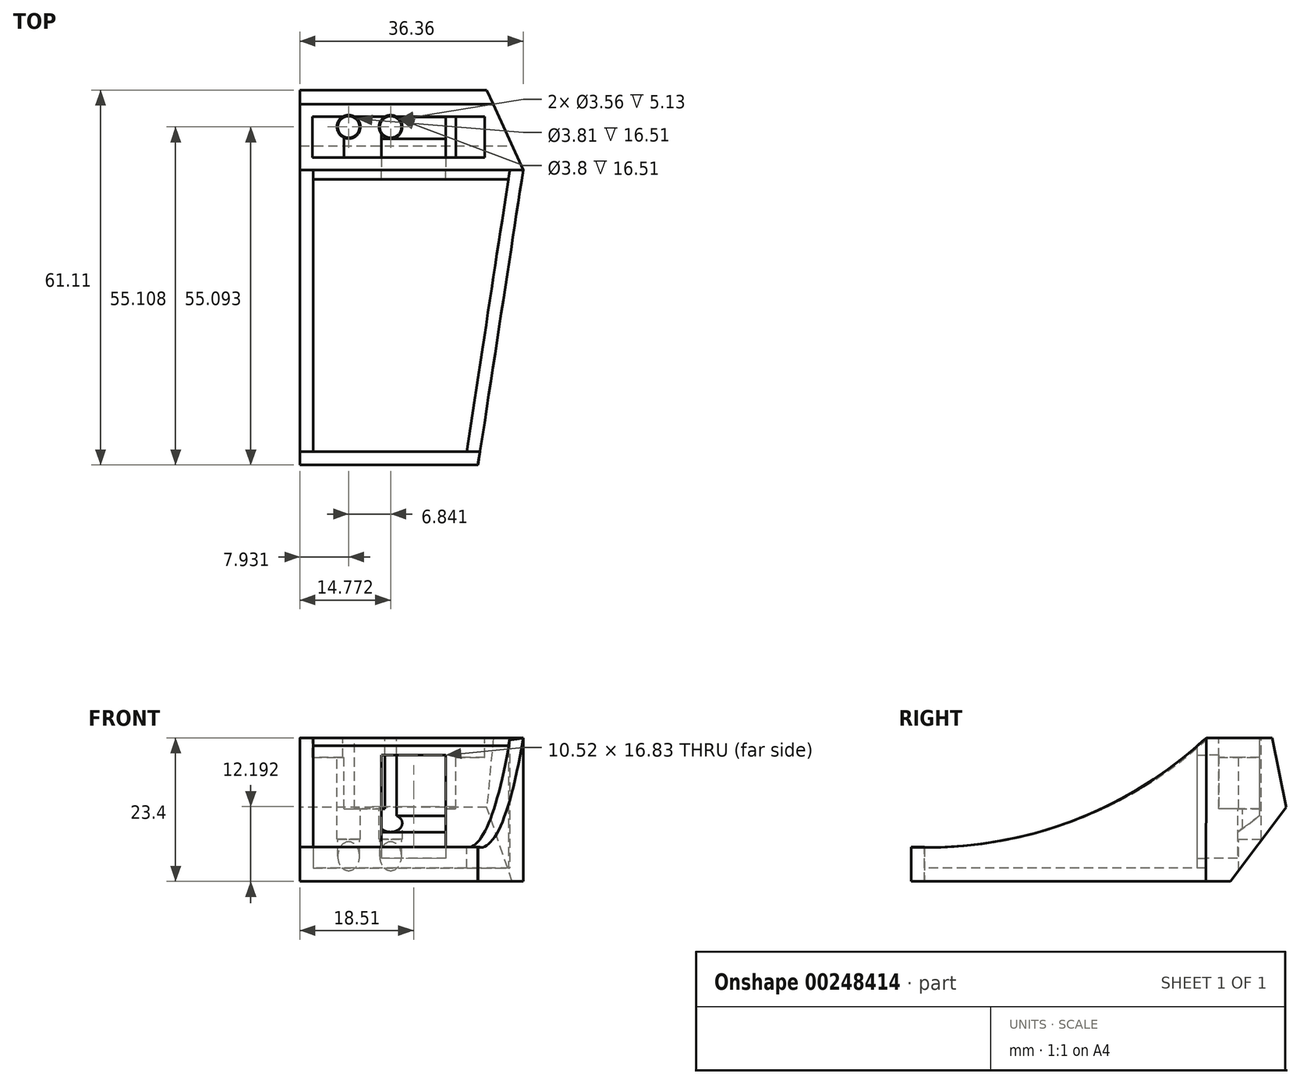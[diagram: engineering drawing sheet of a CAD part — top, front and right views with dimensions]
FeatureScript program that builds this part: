
annotation { "Feature Type Name" : "Feature", "Feature Type Description" : "" }
export const myFeature = defineFeature(function(context is Context, id is Id, definition is map)
    precondition{}
    {
        {
            var Q0;
            Q0=qCreatedBy(makeId("Top.planeOp"),FACE);
            var sketch = newSketch(context, id + "F0", { "sketchPlane" : qUnion([Q0])});
            skLineSegment(sketch, "E0", {"start": v(-18.5, 25.98) * mm, "end": v(-18.5, -25.98) * mm});
            skLineSegment(sketch, "E1", {"start": v(-18.5, -25.98) * mm, "end": v(10.5, -25.98) * mm});
            skLineSegment(sketch, "E2", {"start": v(10.5, -25.98) * mm, "end": v(18.45, 25.98) * mm});
            skLineSegment(sketch, "E3", {"start": v(-18.5, 25.98) * mm, "end": v(18.45, 25.98) * mm});
            skLineSegment(sketch, "E4", {"start": v(0, 0) * mm, "end": v(-18.5, 0) * mm});
            skSolve(sketch);
        }
        {
            var Q0;
            Q0 = qSketchRegion(id + "F0", true);
            extrude(context, id + "F1", {"entities" : qUnion([Q0]), "depth" : 2.16 * mm, "offsetDistance" : 25.4 * mm});
        }
        {
            var Q0;
            Q0=makeQuery(id+"F1.opExtrude","SWEPT_FACE",FACE,{"disambiguationData":[OSD([sQuery(id+"F0.wireOp",EDGE,"E0")])]});
            var sketch = newSketch(context, id + "F2", { "sketchPlane" : qUnion([Q0])});
            skLineSegment(sketch, "E5.MirrorCS", {"start": v(26, 0) * mm, "end": v(26, 5.58) * mm});
            skLineSegment(sketch, "E6.MirrorCS", {"start": v(-22.05, 23.4) * mm, "end": v(-22.05, 0) * mm});
            skLineSegment(sketch, "E7.MirrorCS", {"start": v(-22.05, 23.4) * mm, "end": v(-32.8, 23.38) * mm});
            skLineSegment(sketch, "E8.MirrorCS", {"start": v(-32.8, 23.38) * mm, "end": v(-35.1, 12.1) * mm});
            skLineSegment(sketch, "E9.MirrorCS", {"start": v(-25.98, 0) * mm, "end": v(-35.1, 12.1) * mm});
            skArc(sketch, "E10.MirrorCS", {"start": v(26, 5.58) * mm, "mid": v(0.2, 9.7) * mm, "end": v(-22.05, 23.4) * mm});
            skLineSegment(sketch, "E11.MirrorCS", {"start": v(26, 0) * mm, "end": v(-25.98, 0) * mm});
            skSolve(sketch);
        }
        {
            var Q0;
            {var subQ0=sQuery(id+"F2.wireOp",EDGE,"E11.MirrorCS");var subQ1=sQuery(id+"F2.wireOp",EDGE,"E6.MirrorCS");var subQ2=makeQuery(id+"F2.imprint","INTERSECT",VERTEX,{"derivedFrom":[subQ1,subQ0]});Q0=makeQuery(id+"F2.imprint","IMPRINT",FACE,{"disambiguationData":[TD([[makeQuery(id+"F2.imprint","IMPRINT",EDGE,{"disambiguationData":[TD([[subQ2,1.0]])],"derivedFrom":subQ1}),-1.0]])]});}
            var Q1;
            {var subQ1=sQuery(id+"F0.wireOp",EDGE,"E0");var subQ6=makeQuery(id+"F1.opExtrude","SWEPT_EDGE",EDGE,{"disambiguationData":[OSD([subQ1,sQuery(id+"F0.wireOp",EDGE,"E1")])]});Q1=makeQuery(id+"F2.imprint","IMPRINT",FACE,{"disambiguationData":[TD([[makeQuery(id+"F2.imprint","IMPRINT",EDGE,{"derivedFrom":subQ6}),-1.0]])]});}
            var Q2;
            {var subQ9=sQuery(id+"F2.wireOp",EDGE,"E5.MirrorCS");Q2=makeQuery(id+"F2.imprint","IMPRINT",FACE,{"disambiguationData":[TD([[makeQuery(id+"F2.imprint","IMPRINT",EDGE,{"derivedFrom":subQ9}),1.0]])]});}
            var Q3;
            {var subQ1=sQuery(id+"F0.wireOp",EDGE,"E0");var subQ6=makeQuery(id+"F1.opExtrude","SWEPT_EDGE",EDGE,{"disambiguationData":[OSD([subQ1,sQuery(id+"F0.wireOp",EDGE,"E3")])]});Q3=makeQuery(id+"F2.imprint","IMPRINT",FACE,{"disambiguationData":[TD([[makeQuery(id+"F2.imprint","IMPRINT",EDGE,{"derivedFrom":subQ6}),1.0]])]});}
            extrude(context, id + "F3", {"entities" : qUnion([Q0, Q1, Q2, Q3]), "operationType" : NewBodyOperationType.ADD, "oppositeDirection" : true, "depth" : 2.16 * mm, "offsetDistance" : 25.4 * mm});
        }
        {
            var Q0;
            Q0=makeQuery(id+"F1.opExtrude","SWEPT_FACE",FACE,{"disambiguationData":[OSD([sQuery(id+"F0.wireOp",EDGE,"E2")])]});
            var sketch = newSketch(context, id + "F4", { "sketchPlane" : qUnion([Q0])});
            skLineSegment(sketch, "E12", {"start": v(-24.1, 0) * mm, "end": v(-24.1, 5.58) * mm});
            skLineSegment(sketch, "E13", {"start": v(-24.1, 0) * mm, "end": v(24.54, 0) * mm});
            skLineSegment(sketch, "E14", {"start": v(24.5, 23.39) * mm, "end": v(24.54, 0) * mm});
            skArc(sketch, "E15", {"start": v(-24.1, 5.58) * mm, "mid": v(1.96, 9.68) * mm, "end": v(24.5, 23.39) * mm});
            skSolve(sketch);
        }
        {
            var Q0;
            {var subQ3=sQuery(id+"F4.wireOp",EDGE,"E15");Q0=makeQuery(id+"F4.imprint","IMPRINT",FACE,{"disambiguationData":[TD([[makeQuery(id+"F4.imprint","IMPRINT",EDGE,{"derivedFrom":subQ3}),-1.0]])]});}
            var Q1;
            {var subQ0=sQuery(id+"F4.wireOp",EDGE,"E13");var subQ1=sQuery(id+"F4.wireOp",EDGE,"E12");var subQ2=makeQuery(id+"F4.imprint","INTERSECT",VERTEX,{"derivedFrom":[subQ1,subQ0]});Q1=makeQuery(id+"F4.imprint","IMPRINT",FACE,{"disambiguationData":[TD([[makeQuery(id+"F4.imprint","IMPRINT",EDGE,{"disambiguationData":[TD([[subQ2,1.0]])],"derivedFrom":subQ1}),1.0]])]});}
            extrude(context, id + "F5", {"entities" : qUnion([Q0, Q1]), "operationType" : NewBodyOperationType.ADD, "oppositeDirection" : true, "depth" : 2.16 * mm, "offsetDistance" : 25.4 * mm});
        }
        {
            var Q0;
            {var subQ0=sQuery(id+"F2.wireOp",EDGE,"E7.MirrorCS");Q0=makeQuery(id+"F2.imprint","IMPRINT",FACE,{"disambiguationData":[TD([[makeQuery(id+"F2.imprint","IMPRINT",EDGE,{"derivedFrom":subQ0}),1.0]])]});}
            extrude(context, id + "F6", {"entities" : qUnion([Q0]), "operationType" : NewBodyOperationType.ADD, "oppositeDirection" : true, "depth" : 36.96 * mm, "offsetDistance" : 25.4 * mm});
        }
        {
            var Q0;
            Q0=makeQuery(id+"F6.opExtrude","SWEPT_FACE",FACE,{"disambiguationData":[OSD([sQuery(id+"F2.wireOp",EDGE,"E7.MirrorCS")])]});
            var sketch = newSketch(context, id + "F7", { "sketchPlane" : qUnion([Q0])});
            skLineSegment(sketch, "E16", {"start": v(17.85, 22.01) * mm, "end": v(19.26, 22.01) * mm});
            skLineSegment(sketch, "E17", {"start": v(19.26, 22.01) * mm, "end": v(19.26, 35.65) * mm});
            skLineSegment(sketch, "E18", {"start": v(11.67, 35.65) * mm, "end": v(19.26, 35.65) * mm});
            skLineSegment(sketch, "E19", {"start": v(17.85, 22.01) * mm, "end": v(11.67, 35.65) * mm});
            skSolve(sketch);
        }
        {
            var Q0;
            Q0 = qSketchRegion(id + "F7", true);
            extrude(context, id + "F8", {"entities" : qUnion([Q0]), "operationType" : NewBodyOperationType.REMOVE, "oppositeDirection" : true, "depth" : 25.4 * mm, "offsetDistance" : 25.4 * mm});
        }
        {
            var Q0;
            {var subQ0=sQuery(id+"F0.wireOp",EDGE,"E1");Q0=makeQuery(id+"F0.imprint","IMPRINT",FACE,{"disambiguationData":[TD([[makeQuery(id+"F0.imprint","IMPRINT",EDGE,{"derivedFrom":subQ0}),1.0]])]});}
            var sketch = newSketch(context, id + "F9", { "sketchPlane" : qUnion([Q0])});
            skLineSegment(sketch, "E20", {"start": v(10.45, -26) * mm, "end": v(-18.5, -26) * mm});
            skLineSegment(sketch, "E21", {"start": v(-18.5, -26) * mm, "end": v(-18.5, -23.85) * mm});
            skLineSegment(sketch, "E22", {"start": v(-18.5, -23.85) * mm, "end": v(10.8, -23.85) * mm});
            skLineSegment(sketch, "E23", {"start": v(10.8, -23.85) * mm, "end": v(10.45, -26) * mm});
            skSolve(sketch);
        }
        {
            var Q0;
            Q0 = qSketchRegion(id + "F9", true);
            extrude(context, id + "F10", {"entities" : qUnion([Q0]), "operationType" : NewBodyOperationType.ADD, "depth" : 5.6 * mm, "offsetDistance" : 25.4 * mm});
        }
        {
            var Q0;
            Q0=makeQuery(id+"F6.opExtrude","SWEPT_FACE",FACE,{"disambiguationData":[OSD([sQuery(id+"F2.wireOp",EDGE,"E7.MirrorCS")])]});
            var sketch = newSketch(context, id + "F11", { "sketchPlane" : qUnion([Q0])});
            skLineSegment(sketch, "E24", {"start": v(-18.5, 32.76) * mm, "end": v(12.98, 32.76) * mm});
            skLineSegment(sketch, "E25", {"start": v(12.98, 32.76) * mm, "end": v(17.85, 22.01) * mm});
            skLineSegment(sketch, "E26", {"start": v(17.85, 22.01) * mm, "end": v(-18.5, 22.01) * mm});
            skLineSegment(sketch, "E27", {"start": v(-18.5, 22.01) * mm, "end": v(-18.5, 32.76) * mm});
            skPoint(sketch, "E28.endSnap0", {"position": v(-2.76, 32.76) * mm});
            skLineSegment(sketch, "E29", {"start": v(11.61, 30.72) * mm, "end": v(-16.46, 30.72) * mm});
            skLineSegment(sketch, "E30", {"start": v(-16.46, 30.72) * mm, "end": v(-16.46, 24.05) * mm});
            skLineSegment(sketch, "E31", {"start": v(-16.46, 24.05) * mm, "end": v(11.61, 24.05) * mm});
            skLineSegment(sketch, "E32", {"start": v(11.61, 30.72) * mm, "end": v(11.61, 24.05) * mm});
            skSolve(sketch);
        }
        {
            var Q0;
            Q0=makeQuery(id+"F11.imprint","IMPRINT",FACE,{"disambiguationData":[TD([[makeQuery(id+"F11.imprint","IMPRINT",EDGE,{"derivedFrom":sQuery(id+"F11.wireOp",EDGE,"E29")}),1.0]])]});
            extrude(context, id + "F12", {"entities" : qUnion([Q0]), "operationType" : NewBodyOperationType.REMOVE, "oppositeDirection" : true, "depth" : 3.17 * mm, "offsetDistance" : 25.4 * mm});
        }
        {
            var Q0;
            Q0=makeQuery(id+"F12.boolean.opBoolean","COPY",FACE,{"derivedFrom":makeQuery(id+"F12.opExtrude","CAP_FACE",FACE,{"disambiguationData":[OSD([sQuery(id+"F11.wireOp",EDGE,"E29"),sQuery(id+"F11.wireOp",EDGE,"E30"),sQuery(id+"F11.wireOp",EDGE,"E31"),sQuery(id+"F11.wireOp",EDGE,"E32")])],"isStart":false})});
            var sketch = newSketch(context, id + "F13", { "sketchPlane" : qUnion([Q0])});
            skLineSegment(sketch, "E33", {"start": v(6.89, 24.05) * mm, "end": v(6.89, 30.72) * mm});
            skLineSegment(sketch, "E34", {"start": v(-16.46, 30.72) * mm, "end": v(-11.33, 30.72) * mm});
            skLineSegment(sketch, "E35", {"start": v(-11.33, 30.72) * mm, "end": v(-11.33, 24.05) * mm});
            skLineSegment(sketch, "E36", {"start": v(-11.33, 24.05) * mm, "end": v(6.89, 24.05) * mm});
            skLineSegment(sketch, "E37", {"start": v(-11.33, 30.72) * mm, "end": v(6.89, 30.72) * mm});
            skSolve(sketch);
        }
        {
            var Q0;
            Q0 = qSketchRegion(id + "F13", true);
            extrude(context, id + "F14", {"entities" : qUnion([Q0]), "operationType" : NewBodyOperationType.REMOVE, "oppositeDirection" : true, "depth" : 8.38 * mm, "offsetDistance" : 25.4 * mm});
        }
        {
            var Q0;
            Q0=makeQuery(id+"F6.opExtrude","SWEPT_FACE",FACE,{"disambiguationData":[OSD([sQuery(id+"F2.wireOp",EDGE,"E7.MirrorCS")])]});
            var sketch = newSketch(context, id + "F15", { "sketchPlane" : qUnion([Q0])});
            skCircle(sketch, "E38", {"center": v(-10.58, 29.08) * mm, "radius": 1.78 * mm});
            skCircle(sketch, "E39", {"center": v(-3.74, 29.08) * mm, "radius": 1.78 * mm});
            skSolve(sketch);
        }
        {
            var Q0;
            Q0 = qSketchRegion(id + "F15", true);
            extrude(context, id + "F16", {"entities" : qUnion([Q0]), "operationType" : NewBodyOperationType.REMOVE, "oppositeDirection" : true, "depth" : 25.4 * mm, "offsetDistance" : 25.4 * mm});
        }
        {
            var Q0;
            {var subQ0=sQuery(id+"F2.wireOp",EDGE,"E7.MirrorCS");Q0=makeQuery(id+"F15.imprint","IMPRINT",FACE,{"disambiguationData":[TD([[makeQuery(id+"F15.imprint","IMPRINT",EDGE,{"derivedFrom":makeQuery(id+"F6.opExtrude","CAP_EDGE",EDGE,{"disambiguationData":[OSD([subQ0])],"isStart":true})}),-1.0]])]});}
            var sketch = newSketch(context, id + "F17", { "sketchPlane" : qUnion([Q0])});
            skCircle(sketch, "E40", {"center": v(-10.58, 29.08) * mm, "radius": 1.9 * mm});
            skCircle(sketch, "E41", {"center": v(-3.74, 29.08) * mm, "radius": 1.9 * mm});
            skSolve(sketch);
        }
        {
            var Q0;
            Q0 = qSketchRegion(id + "F17", true);
            extrude(context, id + "F18", {"entities" : qUnion([Q0]), "operationType" : NewBodyOperationType.REMOVE, "oppositeDirection" : true, "depth" : 33.02 * mm, "offsetDistance" : 25.4 * mm, "symmetric" : true});
        }
        {
            var Q0;
            Q0=makeQuery(id+"F6.opExtrude","SWEPT_FACE",FACE,{"disambiguationData":[OSD([sQuery(id+"F2.wireOp",EDGE,"E6.MirrorCS")])]});
            var sketch = newSketch(context, id + "F19", { "sketchPlane" : qUnion([Q0])});
            skLineSegment(sketch, "E42", {"start": v(5.26, 20.6) * mm, "end": v(5.26, 3.78) * mm});
            skLineSegment(sketch, "E43.MirrorCS", {"start": v(-5.26, 20.6) * mm, "end": v(-5.26, 3.78) * mm});
            skLineSegment(sketch, "E44", {"start": v(5.26, 3.78) * mm, "end": v(-5.26, 3.78) * mm});
            skLineSegment(sketch, "E45", {"start": v(5.26, 20.6) * mm, "end": v(-5.26, 20.6) * mm});
            skSolve(sketch);
        }
        {
            var Q0;
            Q0 = qSketchRegion(id + "F19", true);
            extrude(context, id + "F20", {"entities" : qUnion([Q0]), "operationType" : NewBodyOperationType.REMOVE, "oppositeDirection" : true, "depth" : 10.16 * mm, "offsetDistance" : 25.4 * mm, "symmetric" : true});
        }
        {
            var Q0;
            {var subQ0=sQuery(id+"F2.wireOp",EDGE,"E6.MirrorCS");var subQ1=sQuery(id+"F0.wireOp",EDGE,"E3");var subQ2=sQuery(id+"F0.wireOp",EDGE,"E0");Q0=makeQuery(id+"F10.boolean.opBoolean","SPLIT",FACE,{"disambiguationData":[TD([makeQuery(id+"F6.opExtrude","SWEPT_FACE",FACE,{"disambiguationData":[OSD([subQ0])]})])],"derivedFrom":makeQuery(id+"F1.opExtrude","CAP_FACE",FACE,{"disambiguationData":[OSD([subQ2,sQuery(id+"F0.wireOp",EDGE,"E1"),sQuery(id+"F0.wireOp",EDGE,"E2"),subQ1])],"isStart":false})});}
            var sketch = newSketch(context, id + "F21", { "sketchPlane" : qUnion([Q0])});
            skLineSegment(sketch, "E46", {"start": v(15.67, 22.05) * mm, "end": v(-16.34, 22.05) * mm});
            skLineSegment(sketch, "E47", {"start": v(-16.34, 22.05) * mm, "end": v(-16.34, 20.53) * mm});
            skLineSegment(sketch, "E48", {"start": v(-16.34, 20.53) * mm, "end": v(15.44, 20.53) * mm});
            skLineSegment(sketch, "E49", {"start": v(15.44, 20.53) * mm, "end": v(15.67, 22.05) * mm});
            skSolve(sketch);
        }
        {
            var Q0;
            Q0 = qSketchRegion(id + "F21", true);
            extrude(context, id + "F22", {"entities" : qUnion([Q0]), "depth" : 21.23 * mm, "offsetDistance" : 25.4 * mm});
        }
        {
            var Q0;
            Q0=qCreatedBy(makeId("Right.planeOp"),FACE);
            var sketch = newSketch(context, id + "F23", { "sketchPlane" : qUnion([Q0])});
            skLineSegment(sketch, "E50", {"start": v(22.05, 23.4) * mm, "end": v(20.52, 23.4) * mm});
            skLineSegment(sketch, "E51", {"start": v(20.52, 23.4) * mm, "end": v(20.53, 22.1) * mm});
            skArc(sketch, "E52", {"start": v(22.05, 23.4) * mm, "mid": v(21.29, 22.75) * mm, "end": v(20.53, 22.1) * mm});
            skSolve(sketch);
        }
        {
            var Q0;
            Q0 = qSketchRegion(id + "F23", true);
            extrude(context, id + "F24", {"entities" : qUnion([Q0]), "operationType" : NewBodyOperationType.REMOVE, "oppositeDirection" : true, "depth" : 45.72 * mm, "offsetDistance" : 25.4 * mm, "symmetric" : true});
        }
        {
            var Q0;
            Q0=makeQuery(id+"F19.imprint","IMPRINT",FACE,{"disambiguationData":[TD([[makeQuery(id+"F19.imprint","IMPRINT",EDGE,{"derivedFrom":sQuery(id+"F19.wireOp",EDGE,"E42")}),-1.0]])]});
            extrude(context, id + "F25", {"entities" : qUnion([Q0]), "operationType" : NewBodyOperationType.REMOVE, "depth" : 25.4 * mm, "offsetDistance" : 25.4 * mm});
        }
        {
            var Q0;
            {var subQ0=sQuery(id+"F13.wireOp",EDGE,"E36");var subQ1=sQuery(id+"F13.wireOp",EDGE,"E37");var subQ2=sQuery(id+"F13.wireOp",EDGE,"E33");var subQ3=sQuery(id+"F13.wireOp",EDGE,"E35");Q0=makeQuery(id+"F20.boolean.opBoolean","INTERSECT",EDGE,{"derivedFrom":[makeQuery(id+"F16.boolean.opBoolean","SPLIT",FACE,{"disambiguationData":[TD([makeQuery(id+"F12.boolean.opBoolean","COPY",FACE,{"derivedFrom":makeQuery(id+"F12.opExtrude","SWEPT_FACE",FACE,{"disambiguationData":[OSD([sQuery(id+"F11.wireOp",EDGE,"E29")])]})}),makeQuery(id+"F12.boolean.opBoolean","COPY",FACE,{"derivedFrom":makeQuery(id+"F12.opExtrude","SWEPT_FACE",FACE,{"disambiguationData":[OSD([sQuery(id+"F11.wireOp",EDGE,"E31")])]})}),makeQuery(id+"F14.opExtrude","SWEPT_FACE",FACE,{"disambiguationData":[OSD([subQ0])]}),makeQuery(id+"F14.opExtrude","SWEPT_FACE",FACE,{"disambiguationData":[OSD([subQ1])]}),makeQuery(id+"F14.boolean.opBoolean","COPY",FACE,{"derivedFrom":makeQuery(id+"F14.opExtrude","SWEPT_FACE",FACE,{"disambiguationData":[OSD([subQ2])]})}),makeQuery(id+"F14.boolean.opBoolean","COPY",FACE,{"derivedFrom":makeQuery(id+"F14.opExtrude","SWEPT_FACE",FACE,{"disambiguationData":[OSD([subQ3])]})}),makeQuery(id+"F16.opExtrude","SWEPT_FACE",FACE,{"disambiguationData":[OSD([sQuery(id+"F15.wireOp",EDGE,"E38")])]}),makeQuery(id+"F16.opExtrude","SWEPT_FACE",FACE,{"disambiguationData":[OSD([sQuery(id+"F15.wireOp",EDGE,"E39")])]})])],"derivedFrom":makeQuery(id+"F14.boolean.opBoolean","COPY",FACE,{"derivedFrom":makeQuery(id+"F14.opExtrude","CAP_FACE",FACE,{"disambiguationData":[OSD([subQ2,subQ3,subQ0,subQ1])],"isStart":false})})}),makeQuery(id+"F20.opExtrude","CAP_FACE",FACE,{"disambiguationData":[OSD([sQuery(id+"F19.wireOp",EDGE,"E42"),sQuery(id+"F19.wireOp",EDGE,"E43.MirrorCS"),sQuery(id+"F19.wireOp",EDGE,"E44"),sQuery(id+"F19.wireOp",EDGE,"E45")])],"isStart":false})]});}
            chamfer(context, id + "F26", {"entities" : qUnion([Q0]), "chamferType" : ChamferType.OFFSET_ANGLE, "width" : 5.08 * mm, "oppositeDirection" : false, "angle" : 37 * degree, "tangentPropagation" : true});
        }
    });
